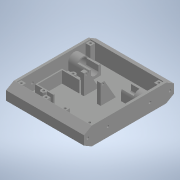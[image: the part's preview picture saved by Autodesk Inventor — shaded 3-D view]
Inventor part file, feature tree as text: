
AUTODESK INVENTOR PART (.ipt)
format: ipt  version: 2020 (Build 240168000, 168)  size: 531,456 bytes
history: native  units: in
note: dims shown in document units (in); Inventor stores cm internally (conversion verified against a paired STEP export)
features: extrude x14, projected_geometry x14, sketch x13, mirror x4, plane x1
ambient origin geometry x8: Origin, YZ Plane, XZ Plane, XY Plane, X Axis, Y Axis, Z Axis, Center Point
bodies: Solid1 (feature_tree)
feature tree (46):
  extrude  "Extrusion1"  Depth=5.9055in
  extrude  "Extrusion2"  TaperAngle=0.0deg  [1 undecoded]
  extrude  "Extrusion3"  Depth=1.063in
  extrude  "Extrusion4"  Depth=0.315in
  extrude  "Extrusion5"  TaperAngle=0.0deg  [1 undecoded]
  extrude  "Extrusion6"  Depth=0.5906in
  mirror  "Mirror1"
  extrude  "Extrusion7"  Depth=0.0787in
  mirror  "Mirror2"
  extrude  "Extrusion8"  Depth=0.6102in
  mirror  "Mirror3"
  plane  "Work Plane1"
  extrude  "Extrusion9"  Depth=0.7874in TaperAngle=0.0deg
  mirror  "Mirror4"
  extrude  "Extrusion10"  Depth=6.063in TaperAngle=0.0deg
  extrude  "Extrusion11"  Depth=0.1575in
  extrude  "Extrusion12"  TaperAngle=0.0deg  [1 undecoded]
  extrude  "Extrusion13"  Depth=0.2756in
  extrude  "Extrusion14"  TaperAngle=0.0deg  [1 undecoded]
  sketch  "Sketch1"  dims[d0=1.1811in d1=5.9055in]
  sketch  "Sketch2"  dims[d2=5.1181in d3=0.0in]
  projected_geometry  "Projected Loop1"
  sketch  "Sketch3"  dims[d4=0.1575in d5=1.063in]
  projected_geometry  "Projected Loop2"
  projected_geometry  "Projected Loop3"
  sketch  "Sketch4"  dims[d6=0.0in d8=0.315in]
  projected_geometry  "Projected Loop4"
  sketch  "Sketch6"  dims[d10=0.993in d11=0.0in]
  sketch  "Sketch7"  dims[d12=0.6496in d13=0.5906in]
  sketch  "Sketch9"  dims[d14=1.5748in d15=0.0787in]
  sketch  "Sketch10"  dims[d16=0.5512in d17=0.0in d18=0.6102in]
  sketch  "Sketch12"  dims[d19=0.4803in d20=0.7874in d21=0.0in]
  projected_geometry  "Projected Loop6"
  projected_geometry  "Projected Loop7"
  projected_geometry  "Projected Loop8"
  sketch  "Sketch13"  dims[d22=0.1654in d23=6.063in d24=0.0in]
  sketch  "Sketch14"  dims[d25=0.5114in d26=0.1575in]
  sketch  "Sketch15"  dims[d27=1.5748in d28=0.0in d29=0.0in]
  projected_geometry  "Projected Loop15"
  sketch  "Sketch16"  dims[d30=0.1575in d31=0.2756in d32=0.0in d33=0.4331in d34=0.122in d38=2.7559in d40=0.061in d41=0.0909in d42=0.2362in d43=0.0in d44=60.0deg d45=0.0787in d46=0.315in d48=0.993in d49=0.0in d53=0.2756in d54=0.0in d55=0.4724in d56=1.2008in d57=1.6142in d58=1.5945in d59=0.0787in d60=0.0787in d62=0.315in d63=0.7677in d64=0.0in d66=0.1476in d67=0.2756in d68=0.0in d69=0.8268in d70=0.2953in d71=0.0394in d72=0.0in d89=0.0157in d90=0.0157in d91=0.1476in d92=0.1476in]
  projected_geometry  "Projected Loop19"
  projected_geometry  "Projected Loop20"
  projected_geometry  "Projected Loop21"
  projected_geometry  "Projected Loop22"
  projected_geometry  "Projected Loop23"
  projected_geometry  "Projected Loop24"
note: 4 required parameter values undecoded (feature->parameter linkage not recoverable at this tier; creation-order binding heuristic only, values carry confidence <= 0.55)
